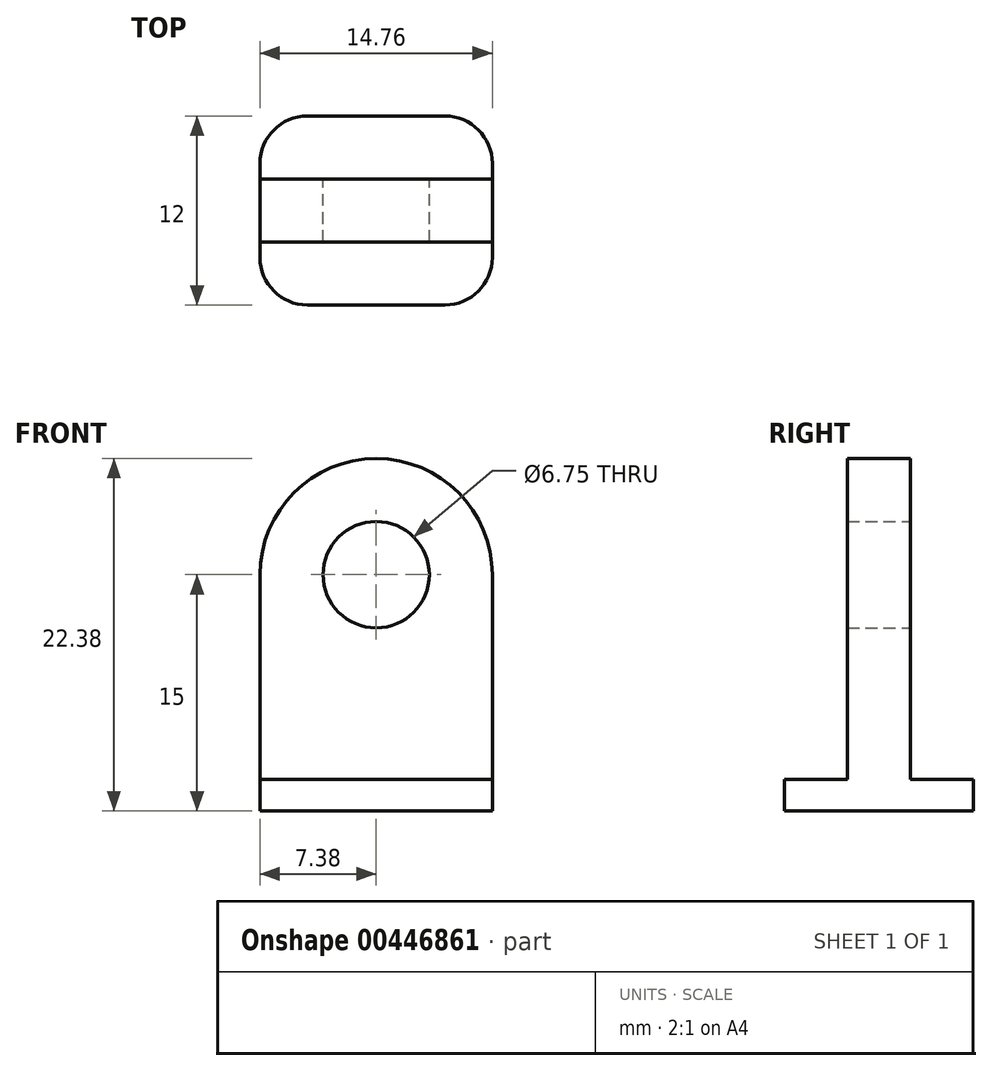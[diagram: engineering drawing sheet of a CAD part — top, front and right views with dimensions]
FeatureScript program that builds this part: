
annotation { "Feature Type Name" : "Feature", "Feature Type Description" : "" }
export const myFeature = defineFeature(function(context is Context, id is Id, definition is map)
    precondition{}
    {
        {
            var Q0;
            Q0=qCreatedBy(makeId("Front.planeOp"),FACE);
            var sketch = newSketch(context, id + "F0", { "sketchPlane" : qUnion([Q0])});
            skCircle(sketch, "E0", {"center": v(0, 0) * mm, "radius": 3.38 * mm});
            skCircle(sketch, "E1", {"center": v(0, 0) * mm, "radius": 7.38 * mm});
            skLineSegment(sketch, "E2", {"start": v(7.37, 0) * mm, "end": v(7.37, -15) * mm});
            skLineSegment(sketch, "E3", {"start": v(-7.38, 0) * mm, "end": v(-7.38, -15) * mm});
            skLineSegment(sketch, "E4", {"start": v(-7.37, -15) * mm, "end": v(7.37, -15) * mm});
            skSolve(sketch);
        }
        {
            var Q0;
            {var subQ0=sQuery(id+"F0.wireOp",EDGE,"E2");Q0=makeQuery(id+"F0.imprint","IMPRINT",FACE,{"disambiguationData":[TD([[makeQuery(id+"F0.imprint","IMPRINT",EDGE,{"derivedFrom":subQ0}),-1.0]])]});}
            var Q1;
            Q1=makeQuery(id+"F0.imprint","IMPRINT",FACE,{"disambiguationData":[TD([[makeQuery(id+"F0.imprint","IMPRINT",EDGE,{"derivedFrom":sQuery(id+"F0.wireOp",EDGE,"E0")}),-1.0]])]});
            extrude(context, id + "F1", {"entities" : qUnion([Q0, Q1]), "depth" : 4 * mm});
        }
        {
            var Q0;
            Q0=makeQuery(id+"F1.opExtrude","SWEPT_FACE",FACE,{"disambiguationData":[OSD([sQuery(id+"F0.wireOp",EDGE,"E4")])]});
            var sketch = newSketch(context, id + "F2", { "sketchPlane" : qUnion([Q0])});
            skLineSegment(sketch, "E5.bottom", {"start": v(-7.37, 4) * mm, "end": v(7.37, 4) * mm});
            skLineSegment(sketch, "E5.top", {"start": v(-7.37, 8) * mm, "end": v(7.37, 8) * mm});
            skLineSegment(sketch, "E5.left", {"start": v(-7.37, 4) * mm, "end": v(-7.37, 8) * mm});
            skLineSegment(sketch, "E5.right", {"start": v(7.37, 4) * mm, "end": v(7.37, 8) * mm});
            skLineSegment(sketch, "E6.bottom", {"start": v(-7.37, 0) * mm, "end": v(7.37, 0) * mm});
            skLineSegment(sketch, "E6.top", {"start": v(-7.37, -4) * mm, "end": v(7.38, -4) * mm});
            skLineSegment(sketch, "E6.left", {"start": v(-7.37, 0) * mm, "end": v(-7.37, -4) * mm});
            skLineSegment(sketch, "E6.right", {"start": v(7.37, 0) * mm, "end": v(7.37, -4) * mm});
            skSolve(sketch);
        }
        {
            var Q0;
            Q0=makeQuery(id+"F2.imprint","IMPRINT",FACE,{"disambiguationData":[TD([[makeQuery(id+"F2.imprint","IMPRINT",EDGE,{"derivedFrom":sQuery(id+"F2.wireOp",EDGE,"E6.bottom")}),-1.0]])]});
            var Q1;
            Q1=makeQuery(id+"F2.imprint","IMPRINT",FACE,{"disambiguationData":[TD([[makeQuery(id+"F2.imprint","IMPRINT",EDGE,{"derivedFrom":sQuery(id+"F2.wireOp",EDGE,"E5.bottom")}),-1.0]])]});
            var Q2;
            Q2=makeQuery(id+"F2.imprint","IMPRINT",FACE,{"disambiguationData":[TD([[makeQuery(id+"F2.imprint","IMPRINT",EDGE,{"derivedFrom":sQuery(id+"F2.wireOp",EDGE,"E5.bottom")}),1.0]])]});
            extrude(context, id + "F3", {"entities" : qUnion([Q0, Q1, Q2]), "operationType" : NewBodyOperationType.ADD, "oppositeDirection" : true, "depth" : 2 * mm});
        }
        {
            var Q0;
            Q0=makeQuery(id+"F3.opExtrude","SWEPT_EDGE",EDGE,{"disambiguationData":[OSD([sQuery(id+"F2.wireOp",EDGE,"E5.top"),sQuery(id+"F2.wireOp",EDGE,"E5.left")])]});
            var Q1;
            Q1=makeQuery(id+"F3.opExtrude","SWEPT_EDGE",EDGE,{"disambiguationData":[OSD([sQuery(id+"F2.wireOp",EDGE,"E5.top"),sQuery(id+"F2.wireOp",EDGE,"E5.right")])]});
            var Q2;
            Q2=makeQuery(id+"F3.opExtrude","SWEPT_EDGE",EDGE,{"disambiguationData":[OSD([sQuery(id+"F2.wireOp",EDGE,"E6.top"),sQuery(id+"F2.wireOp",EDGE,"E6.left")])]});
            var Q3;
            Q3=makeQuery(id+"F3.opExtrude","SWEPT_EDGE",EDGE,{"disambiguationData":[OSD([sQuery(id+"F2.wireOp",EDGE,"E6.top"),sQuery(id+"F2.wireOp",EDGE,"E6.right")])]});
            fillet(context, id + "F4", {"entities" : qUnion([Q0, Q1, Q2, Q3]), "radius" : 3 * mm, "tangentPropagation" : true, "allowEdgeOverflow" : false});
        }
    });
